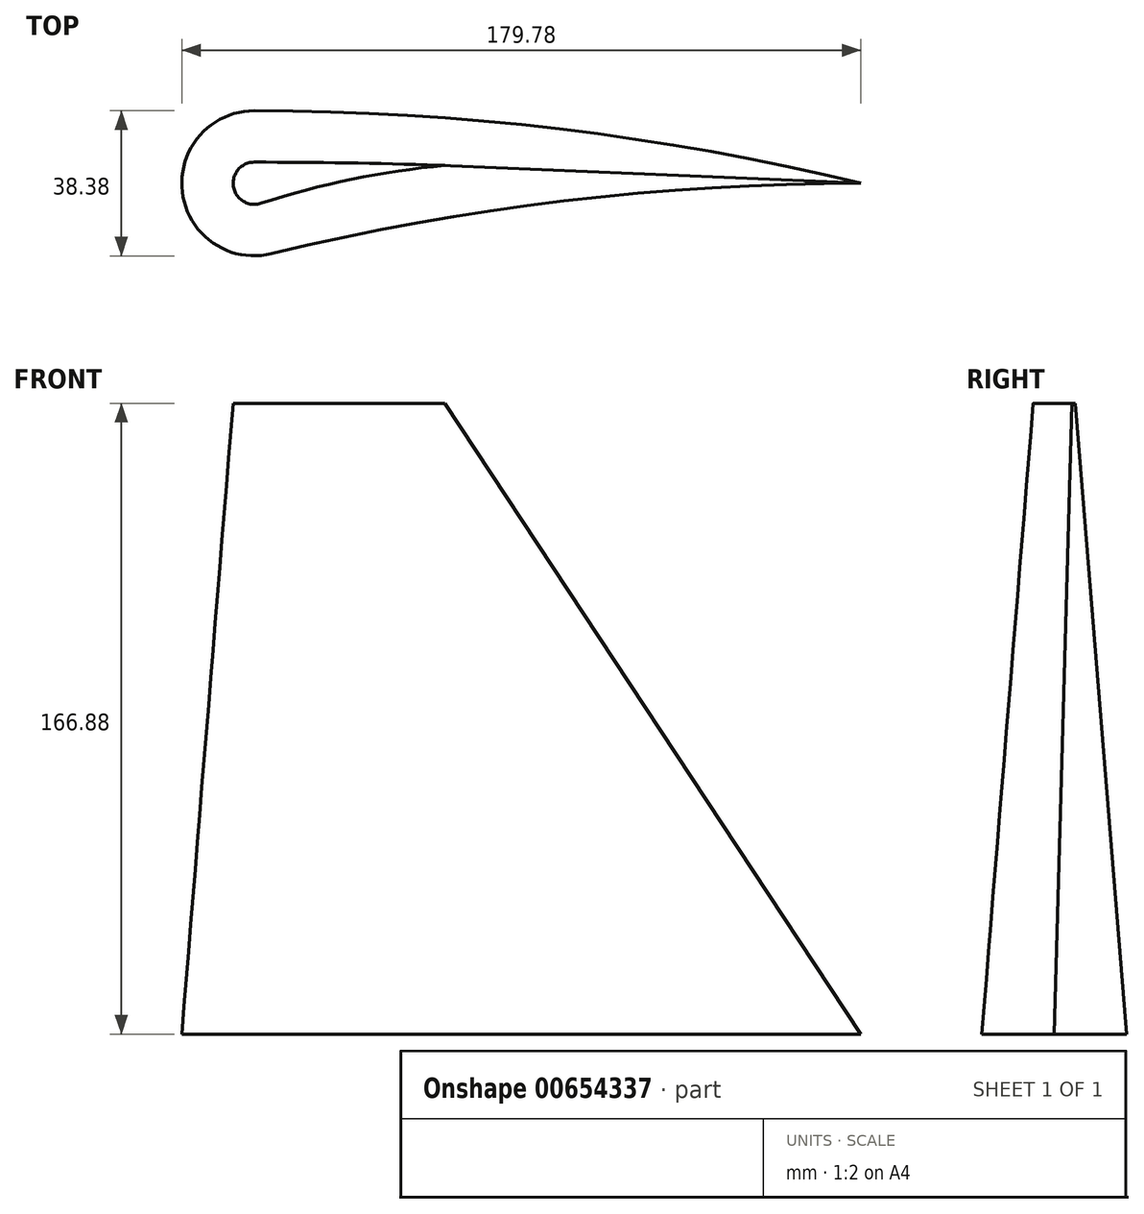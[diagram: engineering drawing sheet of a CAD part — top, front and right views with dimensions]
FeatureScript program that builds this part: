
annotation { "Feature Type Name" : "Feature", "Feature Type Description" : "" }
export const myFeature = defineFeature(function(context is Context, id is Id, definition is map)
    precondition{}
    {
        {
            var Q0;
            Q0=qCreatedBy(makeId("Top.planeOp"),FACE);
            var sketch = newSketch(context, id + "F0", { "sketchPlane" : qUnion([Q0])});
            skArc(sketch, "E0", {"start": v(0, 19.19) * mm, "mid": v(-19.05, -2.28) * mm, "end": v(4.52, -18.65) * mm});
            skLineSegment(sketch, "E1", {"start": v(0, 0) * mm, "end": v(160.59, 0) * mm, "construction": true});
            skArc(sketch, "E2", {"start": v(160.59, 0) * mm, "mid": v(80.86, 14.37) * mm, "end": v(0, 19.19) * mm});
            skArc(sketch, "E3", {"start": v(160.59, 0) * mm, "mid": v(82, -4.68) * mm, "end": v(4.52, -18.65) * mm});
            skSolve(sketch);
        }
        {
            var Q0;
            Q0=qCreatedBy(makeId("Top.planeOp"),FACE);
            cPlane(context, id + "F1", {"entities" : qUnion([Q0]), "cplaneType" : CPlaneType.OFFSET, "offset" : 166.88 * mm, "width" : 152.4 * mm, "height" : 152.4 * mm});
        }
        {
            var Q0;
            Q0=qCreatedBy(id+"F1.planeOp",FACE);
            var sketch = newSketch(context, id + "F2", { "sketchPlane" : qUnion([Q0])});
            skArc(sketch, "E4", {"start": v(0, 5.58) * mm, "mid": v(-5.51, -0.87) * mm, "end": v(1.72, -5.31) * mm});
            skLineSegment(sketch, "E5", {"start": v(0, 0) * mm, "end": v(50.46, 4.72) * mm, "construction": true});
            skArc(sketch, "E6", {"start": v(50.46, 4.72) * mm, "mid": v(25.23, 5.37) * mm, "end": v(0, 5.58) * mm});
            skArc(sketch, "E7", {"start": v(50.46, 4.72) * mm, "mid": v(25.81, 1.04) * mm, "end": v(1.72, -5.31) * mm});
            skSolve(sketch);
        }
        {
            var Q0;
            Q0=makeQuery(id+"F0.imprint","IMPRINT",FACE,{"disambiguationData":[TD([[makeQuery(id+"F0.imprint","IMPRINT",EDGE,{"derivedFrom":sQuery(id+"F0.wireOp",EDGE,"E0")}),1.0]])]});
            var Q1;
            Q1=makeQuery(id+"F2.imprint","IMPRINT",FACE,{"disambiguationData":[TD([[makeQuery(id+"F2.imprint","IMPRINT",EDGE,{"derivedFrom":sQuery(id+"F2.wireOp",EDGE,"E4")}),1.0]])]});
            loft(context, id + "F3", {"sheetProfilesArray" : [{ "sheetProfileEntities" : qUnion([Q0]) }, { "sheetProfileEntities" : qUnion([Q1]) }]});
        }
    });
